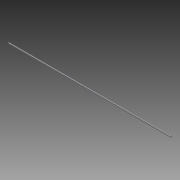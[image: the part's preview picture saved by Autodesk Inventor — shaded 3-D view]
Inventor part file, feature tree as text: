
AUTODESK INVENTOR PART (.ipt)
format: ipt  version: 2013 (Build 170138000, 138)  size: 65,024 bytes
history: native  units: in
note: dims shown in document units (in); Inventor stores cm internally (conversion verified against a paired STEP export)
features: extrude x1, sketch x1
ambient origin geometry x8: Origin, YZ Plane, XZ Plane, XY Plane, X Axis, Y Axis, Z Axis, Center Point
bodies: Solid1 (feature_tree)
feature tree (2):
  extrude  "Extrusion1"  Depth=0.375in
  sketch  "Sketch1"  dims[d0=0.375in d1=0.375in d2=72.0in d3=0.0in]
